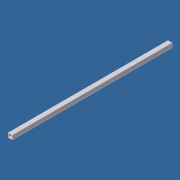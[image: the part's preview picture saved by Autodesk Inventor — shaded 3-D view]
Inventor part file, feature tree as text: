
AUTODESK INVENTOR PART (.ipt)
format: ipt  version: 2012 (Build 160160000, 160)  size: 70,144 bytes
history: native  units: in
note: dims shown in document units (in); Inventor stores cm internally (conversion verified against a paired STEP export)
features: extrude x1, sketch x1
ambient origin geometry x8: Origin, YZ Plane, XZ Plane, XY Plane, X Axis, Y Axis, Z Axis, Center Point
bodies: Solid1 (feature_tree)
feature tree (2):
  extrude  "Extrusion1"  Depth=1.75in
  sketch  "Sketch1"  dims[d0=0.125in d1=1.75in d2=67.0in d3=0.0in]
